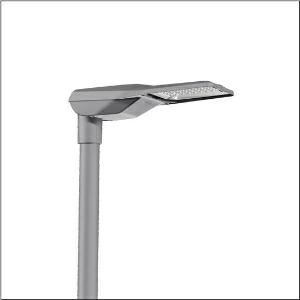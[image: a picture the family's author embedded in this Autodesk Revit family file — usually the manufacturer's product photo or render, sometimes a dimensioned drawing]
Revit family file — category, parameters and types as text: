
# Revit family: streetlight_sl_21_iq_mini___p1_0a_5xe2a41d08hb_633f
name_source: partatom
category: Lighting Fixtures
units: mm (PartAtom-declared; Revit-internal decimal feet)

## family parameters
Cut with Voids When Loaded = No
Host = Face
Light Source = No
Part Type = Normal
Room Calculation Point = No
Round Connector Dimension = Use Diameter
Shared = No

## types (1)
- --- (1 x LED, 9860 lm, 70.9 W, 4000K)
    Apparent Load = 71 VA
    CIE Flux Codes = 21 50 90 100 100
    Color Rendering = 70
    Color Temperature = 4000K
    Default Elevation = 1800 mm
    Description = Streetlight SL 21 iQ mini, mast luminaire, primary light control with lens, of PMMA, primary optical cover: cover, of toughened safety glass, transparent, light distribution: P1.0a, light emission: direct distribution, primary light characteristic: asymmetric, installation type: post-top, side-entry, LED, High Power LED, rated luminous flux: 9.860lm, luminous efficacy: 139lm/W, light colour: 740, colour temperature: 4000K, control: Auto-Match, Temp-Guard, Lumen-Switch, Night-Set, Smart-Wire, Light-Fading, Desk-Remote (wireless, voltage-free reading and setting of iQ features in the workshop via application-optimized NFC function/RFID function), optimised constant luminous flux control (CLO 2.0), presetting dimming linear, mains connection: 220..240V, AC, 50/60Hz, start of lifetime: 71W, end of service life: 75W, reduction: 31W, luminaire housing, of diecast aluminium, powder-coated, Siteco® metallic grey (DB 702S), corrosivity category C5 mid according to DIN EN ISO 12944, please order mast flange separately, inclination adjustable: 0°, 5°, 10°, 15°, sealing non-destructively replaceable, multi-level sealing system, length: 628mm, width: 235mm, height: 110mm, mast flange for spigot size: 42mm (side-entry): 5XC10008XM4, 60/48mm (side-entry/post-top): 5XC10108XM2, 76/60mm (side-entry/post-top): 5XC10108XM1, protection rating (complete): IP66, insulation class (complete): insulation class II (safety insulation), certification: CE, ENEC, ENEC+, VDE, impact resistance: IK09, permissible operating ambient temperature for outdoor applications: -40..+50°C, standard-compliant lighting for roads and squares, packaging unit: 1 piece

Light Distribution: P1.0a
    Height = 110 mm
    Lamp = 1 x LED
    Lamp Light Flux = 9860 lm
    Lamp Power = 70.9 W
    Lamp count = 1
    Length = 625 mm
    Luminous efficacy = 139 lm/W
    Manufacturer = Siteco
    ModVariant = No
    Model = 5XE2A41D08HB
    Number of Poles = 1
    OnlyDefault = Yes
    Power Factor = 1
    Product Name = Streetlight SL 21 iQ mini | P1.0a
    Product group = mast luminaire | pylon top
    ProductGroupID = 6100
    Protection Class = Protection class II
    Protection Degree = IP 66
    RLX_Detail_Level = 1
    RLX_Emergency_Light_Flux = 0 lm
    RLX_Emergency_Type = 0
    RLX_Emergency_Type_DB = No
    RlxData = <blob elided: 103849 chars, md5=7b36a779>
    Socket = socket
    Standby Power = 0 W
    System Light Flux = 9860 lm
    System Power = 71 W
    Type Comments = factory setting: luminous flux: 100 % | dim-lin: 254 | 711 mA
    Type Image = l_1003519.jpg
    URL = http://relux.com
    VarID = @adj_089963
    Voltage = 0 V
    Weight = 0.00 kg
    Width = 234 mm

## geometry (parser evidence)
native form markers: Blend x4, Sweep x11
no freeform markers — native parametric forms only
